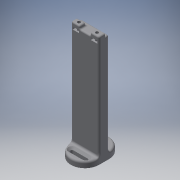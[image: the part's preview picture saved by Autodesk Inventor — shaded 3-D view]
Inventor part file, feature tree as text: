
AUTODESK INVENTOR PART (.ipt)
format: ipt  version: 2016 (Build 200138000, 138)  size: 392,192 bytes
history: native  units: mm
features: extrude x5, sketch x5, fillet x4, plane x2, mirror x2, chamfer x1, projected_geometry x1
ambient origin geometry x8: Origin, YZ Plane, XZ Plane, XY Plane, X Axis, Y Axis, Z Axis, Center Point
bodies: Solid1 (feature_tree)
feature tree (20):
  extrude  "Extrusion1"  Depth=10.0mm
  extrude  "Extrusion2"  Depth=3.0mm
  extrude  "Extrusion3"  Depth=18.0mm
  plane  "Work Plane1"
  mirror  "Mirror1"
  plane  "Work Plane2"
  mirror  "Mirror2"
  extrude  "Extrusion4"  Depth=5.0mm
  extrude  "Extrusion10"  Depth=2.0mm
  chamfer  "Chamfer3"  Distance=5.0mm
  fillet  "Fillet6"  Radius=6.0mm
  fillet  "Fillet1"  Radius=3.0mm
  fillet  "Fillet2"  Radius=2.5mm
  fillet  "Fillet3"  Radius=3.2mm
  sketch  "Sketch1"  dims[d1=10.0mm d2=16.0mm]
  sketch  "Sketch3"  dims[d3=28.0mm d4=3.0mm]
  sketch  "Sketch4"  dims[d5=20.0mm d6=18.0mm]
  sketch  "Sketch5"  dims[d7=3.0mm d8=5.0mm]
  sketch  "Sketch6"  dims[d9=110.0mm d10=0.0mm d25=3.0mm d26=5.0mm d27=6.0mm d28=3.0mm d29=0.0mm d30=2.5mm d31=3.2mm d32=4.0mm d33=6.0mm d34=0.0mm d35=6.0mm d36=0.0mm d37=14.0mm d44=1.4mm d48=1.4mm d49=8.755mm d50=1.4mm d51=14.0mm d66=3.0mm d67=14.0mm d68=9.0mm d69=3.5mm d70=14.0mm d71=6.0mm d72=6.0mm d73=0.0mm d74=2.0mm d75=2.0mm d76=45.0deg d77=2.0mm]
  projected_geometry  "Project Cut Edges1"
